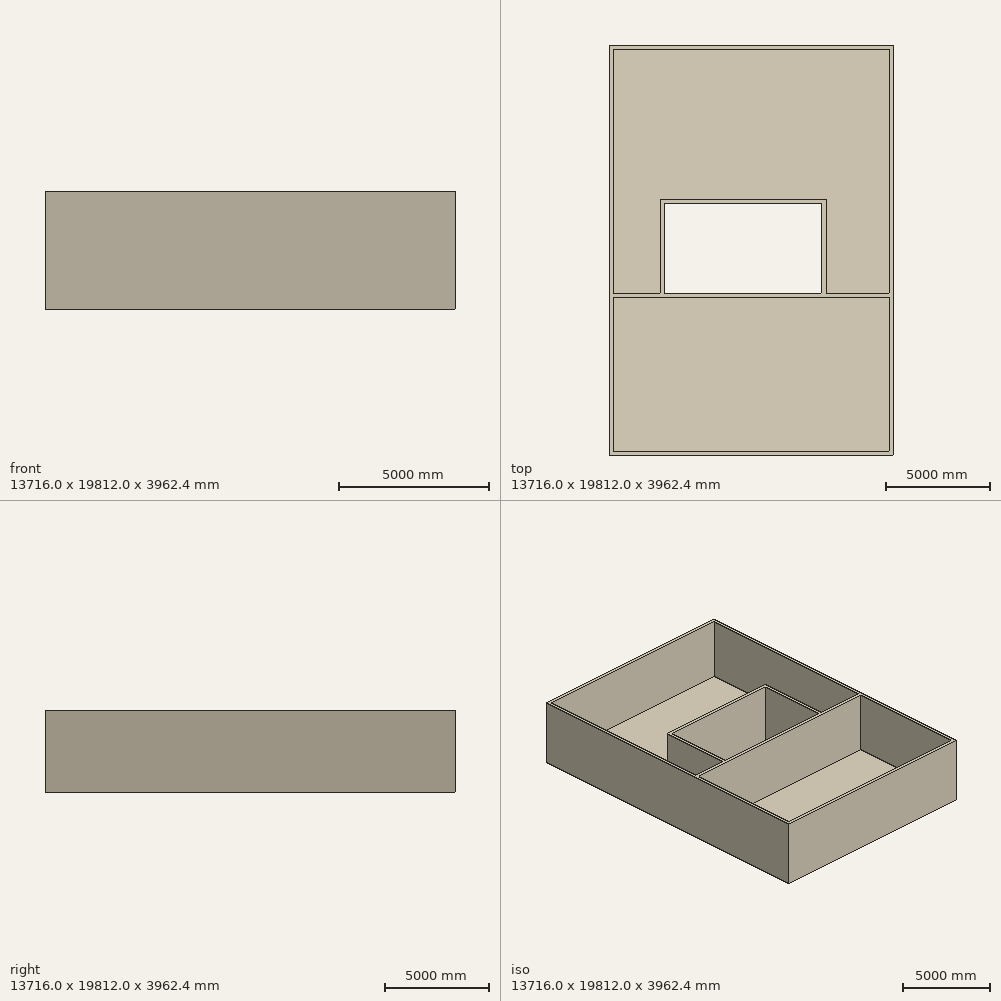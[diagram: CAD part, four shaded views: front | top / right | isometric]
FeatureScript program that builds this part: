
annotation { "Feature Type Name" : "Feature", "Feature Type Description" : "" }
export const myFeature = defineFeature(function(context is Context, id is Id, definition is map)
    precondition{}
    {
        {
            var Q0;
            Q0=qCreatedBy(makeId("Top.planeOp"),FACE);
            var sketch = newSketch(context, id + "F0", { "sketchPlane" : qUnion([Q0])});
            skLineSegment(sketch, "E0.bottom", {"start": v(-6858, 9906) * mm, "end": v(6858, 9906) * mm});
            skLineSegment(sketch, "E0.top", {"start": v(-6858, -9906) * mm, "end": v(6858, -9906) * mm});
            skLineSegment(sketch, "E0.left", {"start": v(-6858, 9906) * mm, "end": v(-6858, -9906) * mm});
            skLineSegment(sketch, "E0.right", {"start": v(6858, 9906) * mm, "end": v(6858, -9906) * mm});
            skPoint(sketch, "E0.middle", {"position": v(0, 0) * mm});
            skLineSegment(sketch, "E1.bottom", {"start": v(-6654.8, 9702.8) * mm, "end": v(6654.8, 9702.8) * mm});
            skLineSegment(sketch, "E1.left", {"start": v(-6654.8, 9702.8) * mm, "end": v(-6654.8, 2082.8) * mm});
            skLineSegment(sketch, "E1.right", {"start": v(6654.8, 9702.8) * mm, "end": v(6654.8, 2082.8) * mm});
            skLineSegment(sketch, "E2.bottom", {"start": v(-6654.8, -2082.8) * mm, "end": v(6654.8, -2082.8) * mm});
            skLineSegment(sketch, "E2.top", {"start": v(-6654.8, -9702.8) * mm, "end": v(6654.8, -9702.8) * mm});
            skLineSegment(sketch, "E2.left", {"start": v(-6654.8, -2082.8) * mm, "end": v(-6654.8, -9702.8) * mm});
            skLineSegment(sketch, "E2.right", {"start": v(6654.8, -2082.8) * mm, "end": v(6654.8, -9702.8) * mm});
            skLineSegment(sketch, "E3.left", {"start": v(-6654.8, 2082.8) * mm, "end": v(-6654.8, -2082.8) * mm});
            skLineSegment(sketch, "E3.right", {"start": v(-4216.4, 2276.84) * mm, "end": v(-4216.4, -2082.8) * mm});
            skLineSegment(sketch, "E4.top", {"start": v(6654.8, -2082.8) * mm, "end": v(3403.6, -2082.8) * mm});
            skLineSegment(sketch, "E4.left", {"start": v(6654.8, 2082.8) * mm, "end": v(6654.8, -2082.8) * mm});
            skLineSegment(sketch, "E4.right", {"start": v(3403.6, 2276.84) * mm, "end": v(3403.6, -2082.8) * mm});
            skLineSegment(sketch, "E5", {"start": v(-4216.4, 2276.84) * mm, "end": v(3403.6, 2276.84) * mm});
            skLineSegment(sketch, "E6", {"start": v(-4419.6, -2082.8) * mm, "end": v(-4419.6, 2480.04) * mm});
            skLineSegment(sketch, "E7", {"start": v(-4419.6, 2480.04) * mm, "end": v(3606.8, 2480.04) * mm});
            skLineSegment(sketch, "E8", {"start": v(3606.8, 2480.04) * mm, "end": v(3606.8, -2082.8) * mm});
            skLineSegment(sketch, "E9", {"start": v(-6654.8, -2286) * mm, "end": v(6654.8, -2286) * mm});
            skSolve(sketch);
        }
        {
            var Q0;
            Q0 = qSketchRegion(id + "F0", true);
            var Q1;
            {var subQ1=sQuery(id+"F0.wireOp",EDGE,"E3.right");Q1=makeQuery(id+"F0.imprint","IMPRINT",FACE,{"disambiguationData":[TD([[makeQuery(id+"F0.imprint","IMPRINT",EDGE,{"derivedFrom":subQ1}),-1.0]])]});}
            var Q2;
            {var subQ3=sQuery(id+"F0.wireOp",EDGE,"E9");Q2=makeQuery(id+"F0.imprint","IMPRINT",FACE,{"disambiguationData":[TD([[makeQuery(id+"F0.imprint","IMPRINT",EDGE,{"derivedFrom":subQ3}),1.0]])]});}
            extrude(context, id + "F1", {"entities" : qUnion([Q0, Q1, Q2]), "depth" : 3657.6 * mm});
        }
        {
            var Q0;
            Q0=makeQuery(id+"F1.opExtrude","CAP_FACE",FACE,{"disambiguationData":[OSD([sQuery(id+"F0.wireOp",EDGE,"E0.bottom"),sQuery(id+"F0.wireOp",EDGE,"E0.top"),sQuery(id+"F0.wireOp",EDGE,"E0.left"),sQuery(id+"F0.wireOp",EDGE,"E0.right"),sQuery(id+"F0.wireOp",EDGE,"E1.bottom"),sQuery(id+"F0.wireOp",EDGE,"E1.left"),sQuery(id+"F0.wireOp",EDGE,"E1.right"),sQuery(id+"F0.wireOp",EDGE,"E2.bottom"),sQuery(id+"F0.wireOp",EDGE,"E2.top"),sQuery(id+"F0.wireOp",EDGE,"E2.left"),sQuery(id+"F0.wireOp",EDGE,"E2.right"),sQuery(id+"F0.wireOp",EDGE,"E3.left"),sQuery(id+"F0.wireOp",EDGE,"E3.right"),sQuery(id+"F0.wireOp",EDGE,"E4.top"),sQuery(id+"F0.wireOp",EDGE,"E4.left"),sQuery(id+"F0.wireOp",EDGE,"E4.right"),sQuery(id+"F0.wireOp",EDGE,"E5"),sQuery(id+"F0.wireOp",EDGE,"E6"),sQuery(id+"F0.wireOp",EDGE,"E7"),sQuery(id+"F0.wireOp",EDGE,"E8"),sQuery(id+"F0.wireOp",EDGE,"E9")])],"isStart":true});
            var sketch = newSketch(context, id + "F2", { "sketchPlane" : qUnion([Q0])});
            skLineSegment(sketch, "E10.bottom", {"start": v(-6858, 9906) * mm, "end": v(6858, 9906) * mm});
            skLineSegment(sketch, "E10.top", {"start": v(-6858, -9906) * mm, "end": v(6858, -9906) * mm});
            skLineSegment(sketch, "E10.left", {"start": v(-6858, 9906) * mm, "end": v(-6858, -9906) * mm});
            skLineSegment(sketch, "E10.right", {"start": v(6858, 9906) * mm, "end": v(6858, -9906) * mm});
            skSolve(sketch);
        }
        {
            var Q0;
            Q0 = qSketchRegion(id + "F2", true);
            extrude(context, id + "F3", {"entities" : qUnion([Q0]), "operationType" : NewBodyOperationType.ADD, "depth" : 304.8 * mm});
        }
        {
            var Q0;
            {var subQ2=sQuery(id+"F0.wireOp",EDGE,"E3.right");Q0=makeQuery(id+"F3.boolean.opBoolean","SPLIT",FACE,{"disambiguationData":[TD([makeQuery(id+"F1.opExtrude","SWEPT_FACE",FACE,{"disambiguationData":[OSD([subQ2])]})])],"derivedFrom":makeQuery(id+"F3.opExtrude","CAP_FACE",FACE,{"disambiguationData":[OSD([sQuery(id+"F2.wireOp",EDGE,"E10.bottom"),sQuery(id+"F2.wireOp",EDGE,"E10.top"),sQuery(id+"F2.wireOp",EDGE,"E10.left"),sQuery(id+"F2.wireOp",EDGE,"E10.right")])],"isStart":true})});}
            var sketch = newSketch(context, id + "F4", { "sketchPlane" : qUnion([Q0])});
            skLineSegment(sketch, "E11.bottom", {"start": v(3403.6, 2276.84) * mm, "end": v(-4216.4, 2276.84) * mm});
            skLineSegment(sketch, "E11.top", {"start": v(3403.6, -2082.8) * mm, "end": v(-4216.4, -2082.8) * mm});
            skLineSegment(sketch, "E11.left", {"start": v(3403.6, 2276.84) * mm, "end": v(3403.6, -2082.8) * mm});
            skLineSegment(sketch, "E11.right", {"start": v(-4216.4, 2276.84) * mm, "end": v(-4216.4, -2082.8) * mm});
            skSolve(sketch);
        }
        {
            var Q0;
            Q0=makeQuery(id+"F4.imprint","IMPRINT",FACE,{"disambiguationData":[TD([[makeQuery(id+"F4.imprint","IMPRINT",EDGE,{"derivedFrom":sQuery(id+"F4.wireOp",EDGE,"E11.bottom")}),-1.0]])]});
            extrude(context, id + "F5", {"entities" : qUnion([Q0]), "operationType" : NewBodyOperationType.REMOVE, "endBound" : BoundingType.THROUGH_ALL, "oppositeDirection" : true, "depth" : 304.8 * mm});
        }
    });
